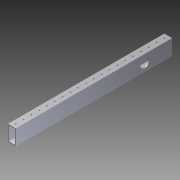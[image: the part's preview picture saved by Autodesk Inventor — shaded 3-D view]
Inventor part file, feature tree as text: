
AUTODESK INVENTOR PART (.ipt)
format: ipt  version: 2014 SP1 (Build 180222100, 222)  size: 773,120 bytes
history: native  units: in
note: dims shown in document units (in); Inventor stores cm internally (conversion verified against a paired STEP export)
features: extrude x3, sketch x3, other x2, imported_body x1
ambient origin geometry x8: Origin, YZ Plane, XZ Plane, XY Plane, X Axis, Y Axis, Z Axis, Center Point
bodies: Body1 (feature_tree)
feature tree (9):
  other  "Cut-Extrude2"
  other  "2x1 Tube1"
  extrude  "Extrusion1"  Depth=1.125in
  extrude  "Extrusion2"  Depth=2.0in TaperAngle=0.0deg
  extrude  "Extrusion3"  Depth=2.0in
  imported_body  "Base1"
  sketch  "Sketch1"  dims[d0=39.0in d1=0.0in d2=1.125in]
  sketch  "Sketch2"  dims[d3=3.5in d4=2.0in d5=0.0in]
  sketch  "Sketch4"  dims[d6=1.125in d7=3.5in d8=2.0in d9=0.0in]
